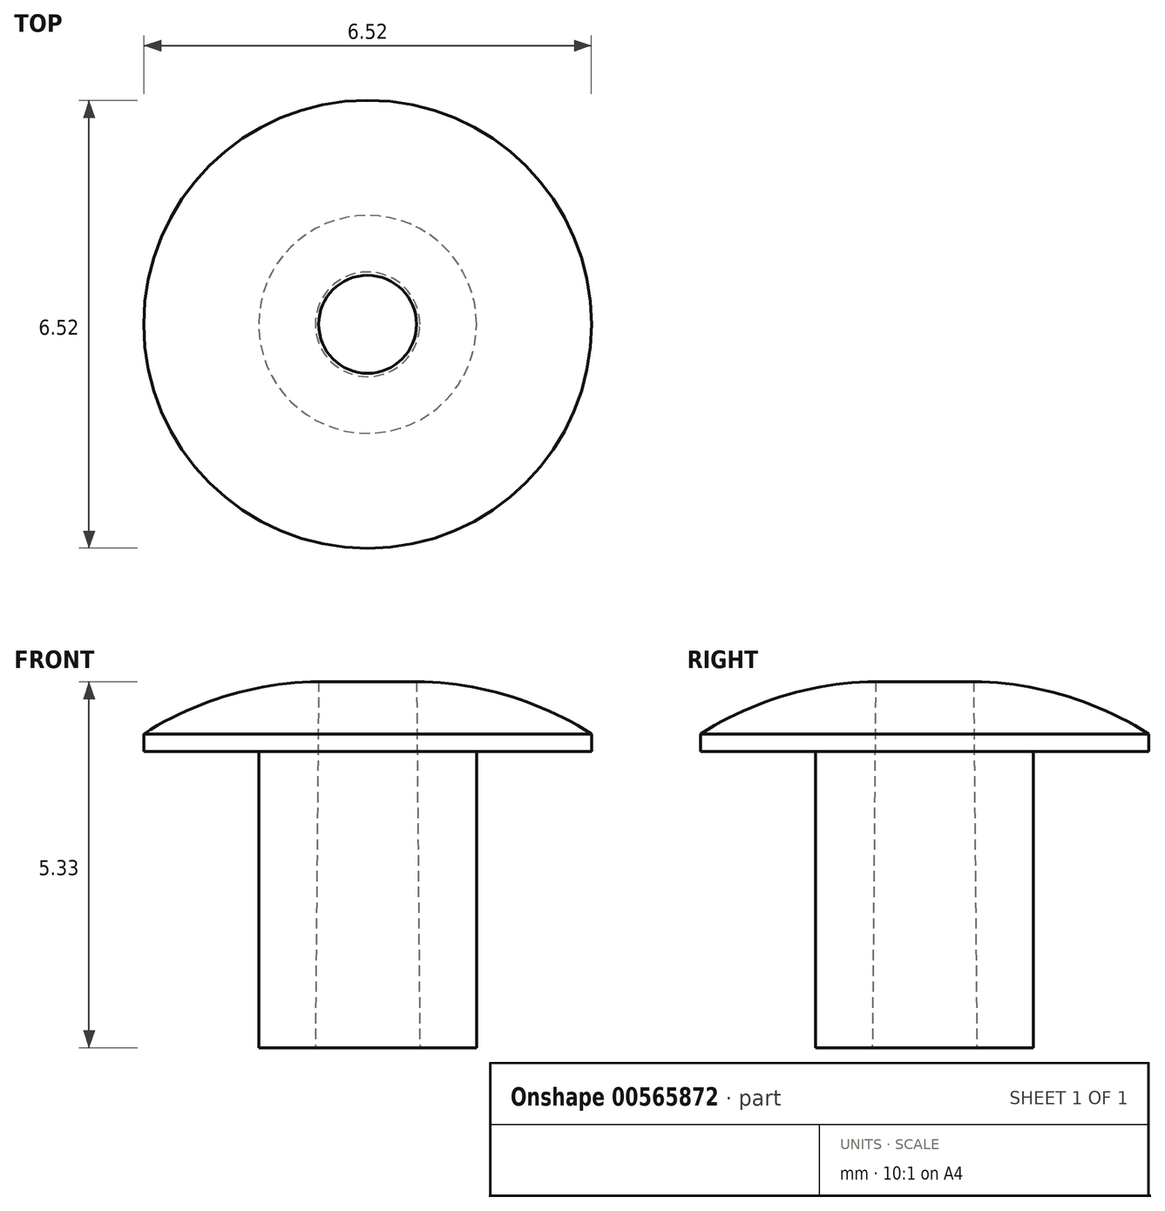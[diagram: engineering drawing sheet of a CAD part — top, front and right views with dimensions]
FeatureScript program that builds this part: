
annotation { "Feature Type Name" : "Feature", "Feature Type Description" : "" }
export const myFeature = defineFeature(function(context is Context, id is Id, definition is map)
    precondition{}
    {
        {
            var Q0;
            Q0=qCreatedBy(makeId("Front.planeOp"),FACE);
            var sketch = newSketch(context, id + "F0", { "sketchPlane" : qUnion([Q0])});
            skLineSegment(sketch, "E0", {"start": v(0, 3.03) * mm, "end": v(0, -2.04) * mm});
            skLineSegment(sketch, "E1", {"start": v(0.76, -2.04) * mm, "end": v(1.59, -2.04) * mm});
            skLineSegment(sketch, "E2", {"start": v(1.59, -2.04) * mm, "end": v(1.59, 2.28) * mm});
            skLineSegment(sketch, "E3", {"start": v(1.59, 2.28) * mm, "end": v(3.26, 2.28) * mm});
            skLineSegment(sketch, "E4", {"start": v(3.26, 2.28) * mm, "end": v(3.26, 2.53) * mm});
            skPoint(sketch, "E5.orphan", {"position": v(0, 3.01) * mm});
            skPoint(sketch, "E6.orphan", {"position": v(-1.38, 3.01) * mm});
            skLineSegment(sketch, "E7", {"start": v(0.71, 3.3) * mm, "end": v(0.76, -2.04) * mm});
            skArc(sketch, "E8", {"start": v(3.26, 2.53) * mm, "mid": v(2.04, 3.1) * mm, "end": v(0.71, 3.3) * mm});
            skSolve(sketch);
        }
        {
            var Q0;
            Q0=makeQuery(id+"F0.imprint","IMPRINT",FACE,{"disambiguationData":[TD([[makeQuery(id+"F0.imprint","IMPRINT",EDGE,{"derivedFrom":sQuery(id+"F0.wireOp",EDGE,"E1")}),1.0]])]});
            var Q1;
            Q1=sQuery(id+"F0.wireOp",EDGE,"E0");
            revolve(context, id + "F1", {"entities" : qUnion([Q0]), "axis" : qUnion([Q1]), "revolveType" : RevolveType.FULL});
        }
    });
